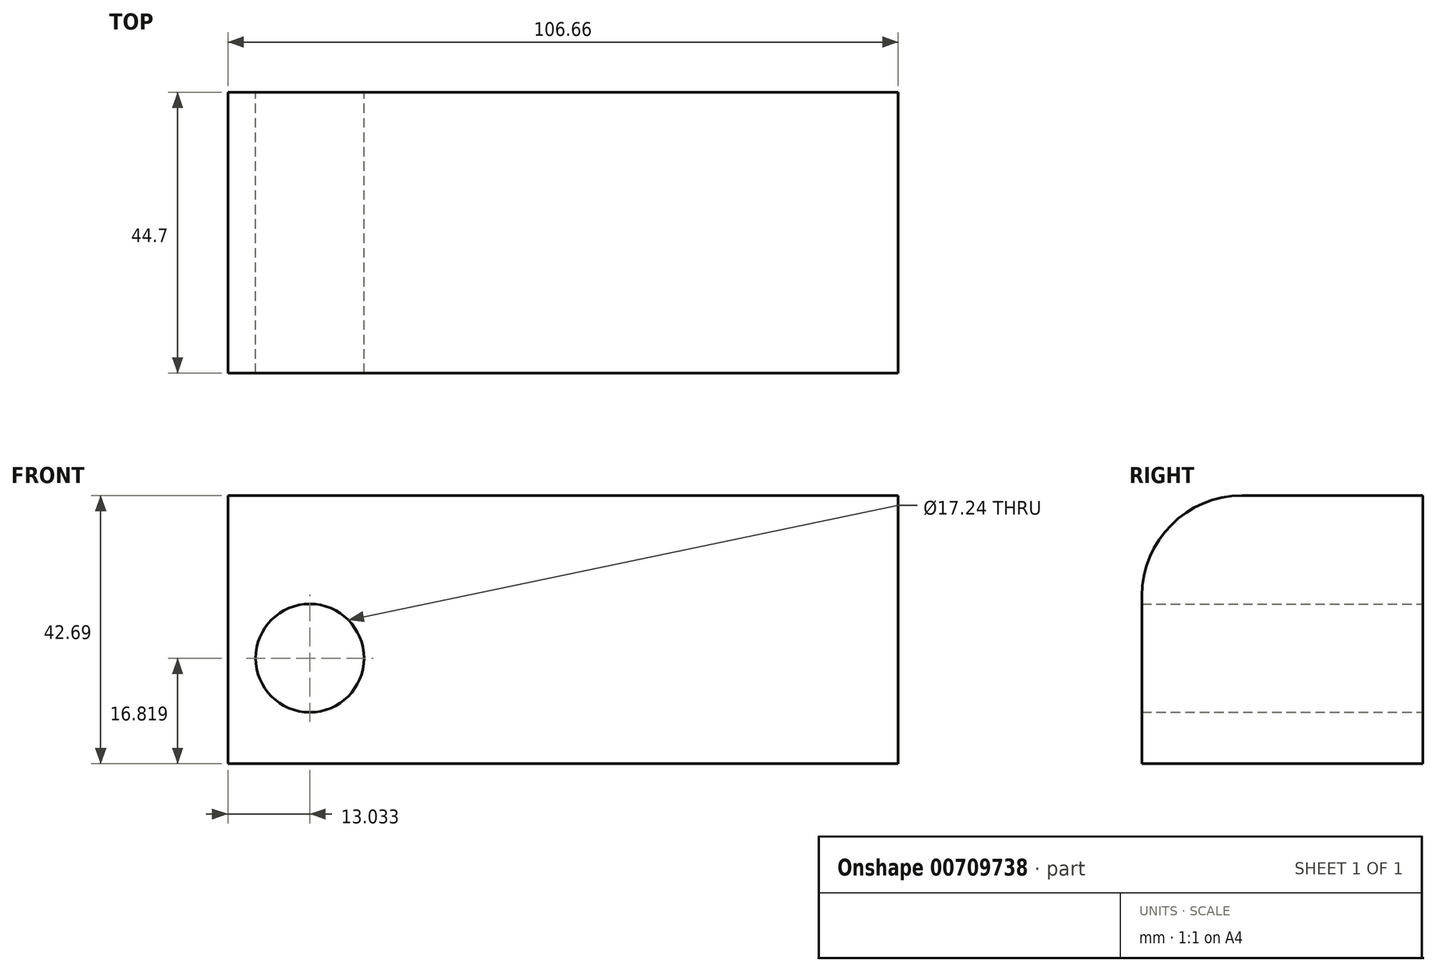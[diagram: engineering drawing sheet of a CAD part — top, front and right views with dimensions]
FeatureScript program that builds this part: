
annotation { "Feature Type Name" : "Feature", "Feature Type Description" : "" }
export const myFeature = defineFeature(function(context is Context, id is Id, definition is map)
    precondition{}
    {
        {
            var Q0;
            Q0=qCreatedBy(makeId("Front.planeOp"),FACE);
            var sketch = newSketch(context, id + "F0", { "sketchPlane" : qUnion([Q0])});
            skLineSegment(sketch, "E0.bottom", {"start": v(-71.7, 5.38) * mm, "end": v(34.96, 5.38) * mm});
            skLineSegment(sketch, "E0.top", {"start": v(-71.7, -37.31) * mm, "end": v(34.96, -37.31) * mm});
            skLineSegment(sketch, "E0.left", {"start": v(-71.7, 5.38) * mm, "end": v(-71.7, -37.31) * mm});
            skLineSegment(sketch, "E0.right", {"start": v(34.96, 5.38) * mm, "end": v(34.96, -37.31) * mm});
            skCircle(sketch, "E1", {"center": v(-58.67, -20.5) * mm, "radius": 8.62 * mm});
            skSolve(sketch);
        }
        {
            var Q0;
            Q0=makeQuery(id+"F0.imprint","IMPRINT",FACE,{"disambiguationData":[TD([[makeQuery(id+"F0.imprint","IMPRINT",EDGE,{"derivedFrom":sQuery(id+"F0.wireOp",EDGE,"E0.bottom")}),-1.0]])]});
            extrude(context, id + "F1", {"entities" : qUnion([Q0]), "depth" : 44.7 * mm, "offsetDistance" : 25.4 * mm});
        }
        {
            var Q0;
            Q0=makeQuery(id+"F1.opExtrude","CAP_EDGE",EDGE,{"disambiguationData":[OSD([sQuery(id+"F0.wireOp",EDGE,"E0.bottom")])],"isStart":false});
            fillet(context, id + "F2", {"entities" : qUnion([Q0]), "radius" : 15.94 * mm, "tangentPropagation" : true, "allowEdgeOverflow" : false});
        }
    });
